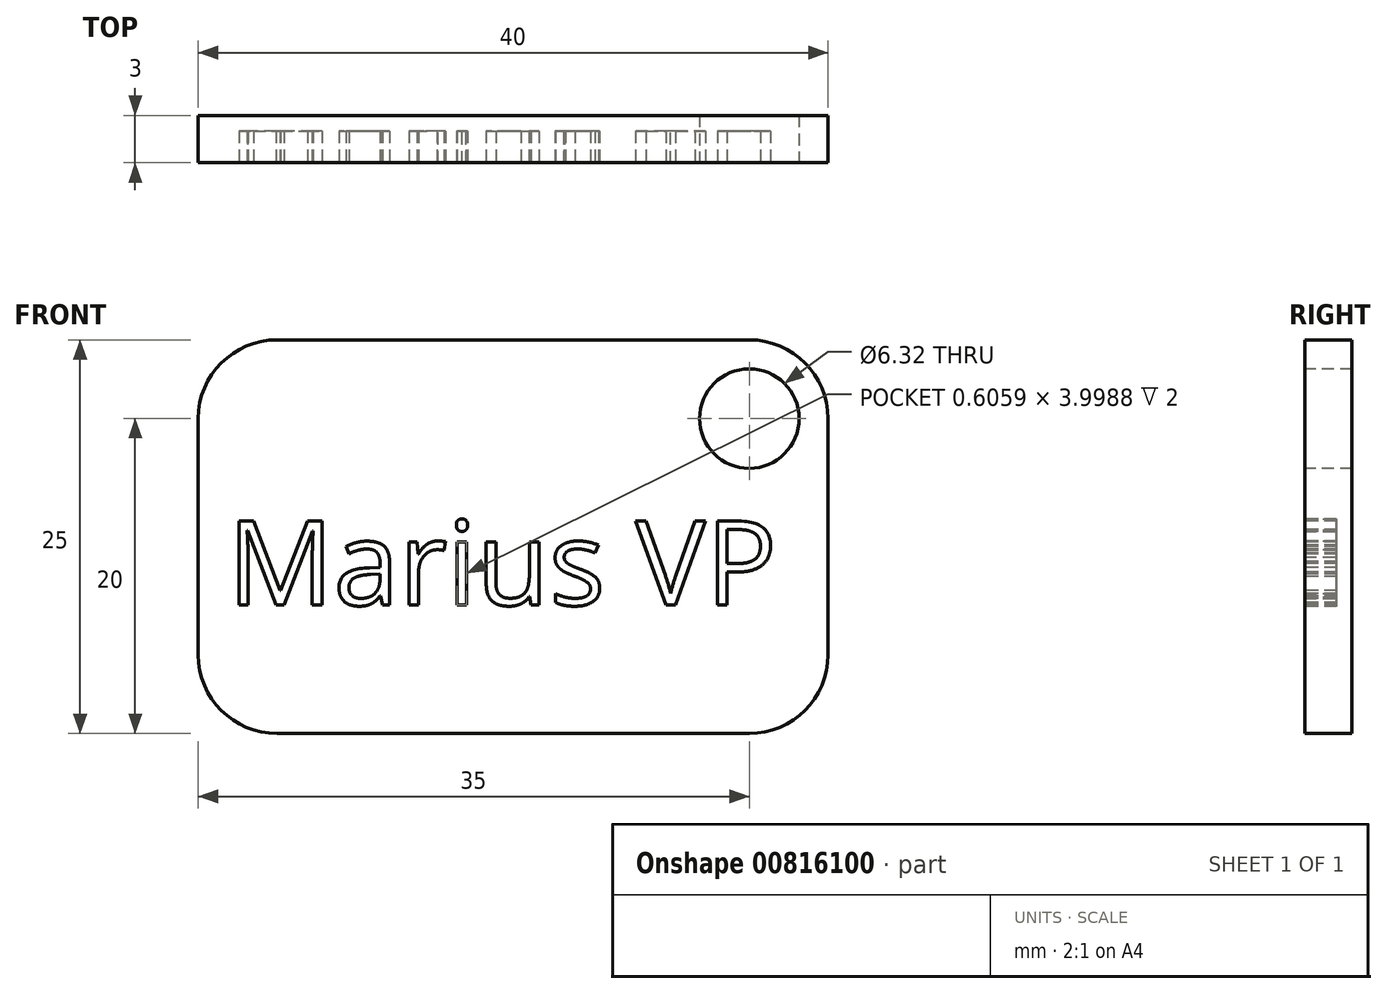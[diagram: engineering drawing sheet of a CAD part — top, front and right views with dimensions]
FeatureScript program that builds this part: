
annotation { "Feature Type Name" : "Feature", "Feature Type Description" : "" }
export const myFeature = defineFeature(function(context is Context, id is Id, definition is map)
    precondition{}
    {
        {
            var Q0;
            Q0=qCreatedBy(makeId("Front.planeOp"),FACE);
            var sketch = newSketch(context, id + "F0", { "sketchPlane" : qUnion([Q0])});
            skLineSegment(sketch, "E0.bottom", {"start": v(5, 0) * mm, "end": v(35, 0) * mm});
            skLineSegment(sketch, "E0.top", {"start": v(5, 25) * mm, "end": v(35, 25) * mm});
            skLineSegment(sketch, "E0.left", {"start": v(0, 5) * mm, "end": v(0, 20) * mm});
            skLineSegment(sketch, "E0.right", {"start": v(40, 5) * mm, "end": v(40, 20) * mm});
            skPoint(sketch, "E1.visualSharp", {"position": v(0, 25) * mm});
            skArc(sketch, "E1.filletArc", {"start": v(5, 25) * mm, "mid": v(1.46, 23.54) * mm, "end": v(0, 20) * mm});
            skPoint(sketch, "E2.visualSharp", {"position": v(40, 25) * mm});
            skArc(sketch, "E2.filletArc", {"start": v(40, 20) * mm, "mid": v(38.54, 23.54) * mm, "end": v(35, 25) * mm});
            skPoint(sketch, "E3.visualSharp", {"position": v(40, 0) * mm});
            skArc(sketch, "E3.filletArc", {"start": v(35, 0) * mm, "mid": v(38.54, 1.46) * mm, "end": v(40, 5) * mm});
            skPoint(sketch, "E4.visualSharp", {"position": v(0, 0) * mm});
            skArc(sketch, "E4.filletArc", {"start": v(0, 5) * mm, "mid": v(1.46, 1.46) * mm, "end": v(5, 0) * mm});
            skSolve(sketch);
        }
        {
            var Q0;
            Q0 = qSketchRegion(id + "F0", true);
            extrude(context, id + "F1", {"entities" : qUnion([Q0]), "depth" : 3 * mm, "offsetDistance" : 25 * mm});
        }
        {
            var Q0;
            Q0=makeQuery(id+"F1.opExtrude","CAP_FACE",FACE,{"disambiguationData":[OSD([sQuery(id+"F0.wireOp",EDGE,"E0.bottom"),sQuery(id+"F0.wireOp",EDGE,"E0.top"),sQuery(id+"F0.wireOp",EDGE,"E0.left"),sQuery(id+"F0.wireOp",EDGE,"E0.right"),sQuery(id+"F0.wireOp",EDGE,"E1.filletArc"),sQuery(id+"F0.wireOp",EDGE,"E2.filletArc"),sQuery(id+"F0.wireOp",EDGE,"E3.filletArc"),sQuery(id+"F0.wireOp",EDGE,"E4.filletArc")])],"isStart":false});
            var sketch = newSketch(context, id + "F2", { "sketchPlane" : qUnion([Q0])});
            skCircle(sketch, "E5", {"center": v(35, 20) * mm, "radius": 3.16 * mm});
            skSolve(sketch);
        }
        {
            var Q0;
            Q0 = qSketchRegion(id + "F2", true);
            extrude(context, id + "F3", {"entities" : qUnion([Q0]), "operationType" : NewBodyOperationType.REMOVE, "oppositeDirection" : true, "depth" : 3 * mm, "offsetDistance" : 25 * mm});
        }
        {
            var Q0;
            Q0=makeQuery(id+"F1.opExtrude","CAP_FACE",FACE,{"disambiguationData":[OSD([sQuery(id+"F0.wireOp",EDGE,"E0.bottom"),sQuery(id+"F0.wireOp",EDGE,"E0.top"),sQuery(id+"F0.wireOp",EDGE,"E0.left"),sQuery(id+"F0.wireOp",EDGE,"E0.right"),sQuery(id+"F0.wireOp",EDGE,"E1.filletArc"),sQuery(id+"F0.wireOp",EDGE,"E2.filletArc"),sQuery(id+"F0.wireOp",EDGE,"E3.filletArc"),sQuery(id+"F0.wireOp",EDGE,"E4.filletArc")])],"isStart":false});
            var sketch = newSketch(context, id + "F4", { "sketchPlane" : qUnion([Q0])});
            skText(sketch, "E6", { "text": "Marius VP", "fontName": "OpenSans-Regular.ttf"});
            const initialGuessF4  = {"E6": [0.00185, 0.00815, 1, 0, 0.00538]};
            skSetInitialGuess(sketch, initialGuessF4);
            skSolve(sketch);
        }
        {
            var Q0;
            Q0 = qSketchRegion(id + "F4", true);
            extrude(context, id + "F5", {"entities" : qUnion([Q0]), "operationType" : NewBodyOperationType.REMOVE, "oppositeDirection" : true, "depth" : 2 * mm, "offsetDistance" : 25 * mm});
        }
    });
